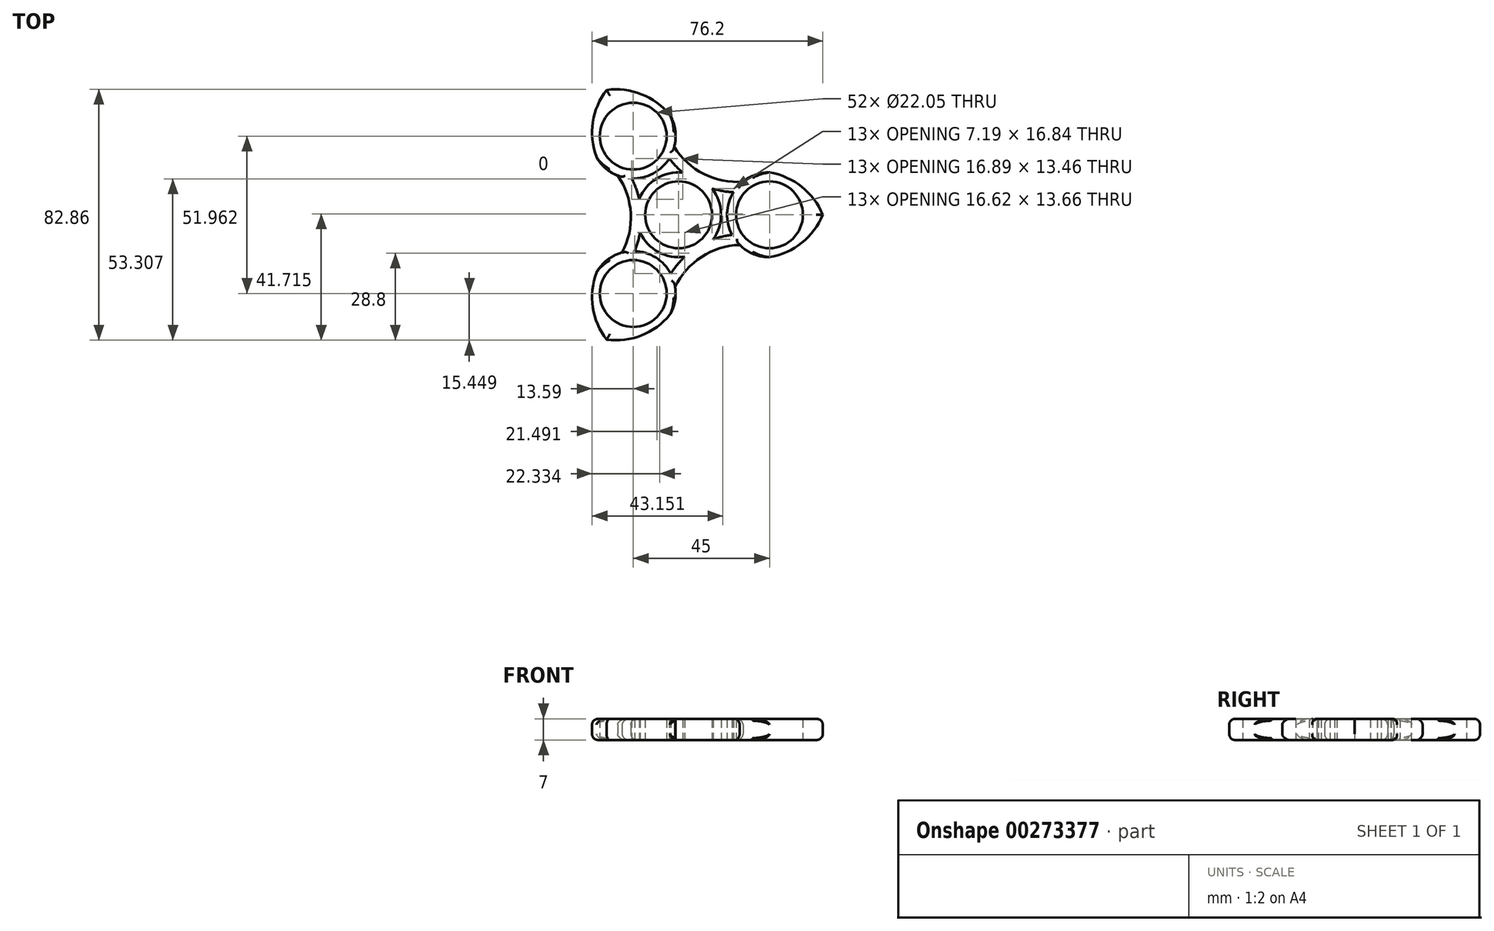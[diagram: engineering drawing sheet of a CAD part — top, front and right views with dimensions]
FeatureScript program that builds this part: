
annotation { "Feature Type Name" : "Feature", "Feature Type Description" : "" }
export const myFeature = defineFeature(function(context is Context, id is Id, definition is map)
    precondition{}
    {
        {
            var Q0;
            Q0=qCreatedBy(makeId("Top.planeOp"),FACE);
            var sketch = newSketch(context, id + "F0", { "sketchPlane" : qUnion([Q0])});
            skCircle(sketch, "E0", {"center": v(0, 0) * mm, "radius": 11.03 * mm});
            skCircle(sketch, "E1", {"center": v(30, 0) * mm, "radius": 11.03 * mm});
            skArc(sketch, "E2", {"start": v(11.4, -8.13) * mm, "mid": v(14, 0.36) * mm, "end": v(10.97, 8.7) * mm});
            skArc(sketch, "E3", {"start": v(30, 14) * mm, "mid": v(25.38, 13.22) * mm, "end": v(21.28, 10.95) * mm});
            skArc(sketch, "E4", {"start": v(47.61, 0) * mm, "mid": v(40.61, 9.27) * mm, "end": v(30, 14) * mm});
            skArc(sketch, "E5.MirrorCS", {"start": v(47.61, 0) * mm, "mid": v(40.61, -9.27) * mm, "end": v(30, -14) * mm});
            skArc(sketch, "E6.1.0", {"start": v(-27.12, 18.98) * mm, "mid": v(-24.14, 15.37) * mm, "end": v(-20.12, 12.95) * mm});
            skArc(sketch, "E6.1.1", {"start": v(-23.8, 41.23) * mm, "mid": v(-12.28, 39.8) * mm, "end": v(-2.88, 32.98) * mm});
            skCircle(sketch, "E6.1.2", {"center": v(-15, 25.98) * mm, "radius": 11.03 * mm});
            skArc(sketch, "E6.1.3", {"start": v(-23.8, 41.23) * mm, "mid": v(-28.34, 30.54) * mm, "end": v(-27.12, 18.98) * mm});
            skArc(sketch, "E6.2.0", {"start": v(-2.88, -32.98) * mm, "mid": v(-1.25, -28.59) * mm, "end": v(-1.15, -23.9) * mm});
            skArc(sketch, "E6.2.1", {"start": v(-23.8, -41.23) * mm, "mid": v(-28.34, -30.54) * mm, "end": v(-27.12, -18.98) * mm});
            skCircle(sketch, "E6.2.2", {"center": v(-15, -25.98) * mm, "radius": 11.03 * mm});
            skArc(sketch, "E6.2.3", {"start": v(-23.8, -41.23) * mm, "mid": v(-12.28, -39.8) * mm, "end": v(-2.88, -32.98) * mm});
            skArc(sketch, "E7.0", {"start": v(21.12, -6.42) * mm, "mid": v(21.08, -6.42) * mm, "end": v(21.03, -6.42) * mm});
            skArc(sketch, "E8.trimOffspring", {"start": v(17.66, -6.62) * mm, "mid": v(14.49, -7.2) * mm, "end": v(11.4, -8.13) * mm});
            skArc(sketch, "E9.trimOffspring", {"start": v(20.15, -9.95) * mm, "mid": v(24.68, -12.95) * mm, "end": v(30, -14) * mm});
            skArc(sketch, "E10.trimOffspring", {"start": v(-2.61, -19.46) * mm, "mid": v(-7.58, -14.1) * mm, "end": v(-14.57, -11.99) * mm});
            skArc(sketch, "E11.trimOffspring", {"start": v(2.05, -13.85) * mm, "mid": v(-0.46, -16.5) * mm, "end": v(-2.61, -19.46) * mm});
            skArc(sketch, "E12.1.0", {"start": v(10.97, 8.7) * mm, "mid": v(14.52, 7.85) * mm, "end": v(18.16, 7.47) * mm});
            skArc(sketch, "E12.1.2", {"start": v(-3.1, 18.6) * mm, "mid": v(-1.01, 16.14) * mm, "end": v(1.35, 13.94) * mm});
            skArc(sketch, "E12.2.0", {"start": v(-13.02, 5.15) * mm, "mid": v(-14.06, 8.65) * mm, "end": v(-15.54, 12) * mm});
            skArc(sketch, "E12.2.2", {"start": v(-14.57, -11.99) * mm, "mid": v(-13.47, -8.95) * mm, "end": v(-12.74, -5.8) * mm});
            skArc(sketch, "E13.trimOffspring", {"start": v(-12.74, -5.8) * mm, "mid": v(-6.69, -12.3) * mm, "end": v(2.05, -13.85) * mm});
            skArc(sketch, "E14.trimOffspring", {"start": v(1.35, 13.94) * mm, "mid": v(-7.3, 11.94) * mm, "end": v(-13.02, 5.15) * mm});
            skArc(sketch, "E15.trimOffspring", {"start": v(-15.54, 12) * mm, "mid": v(-8.43, 13.62) * mm, "end": v(-3.1, 18.6) * mm});
            skArc(sketch, "E16.trimOffspring", {"start": v(-1.46, 22.43) * mm, "mid": v(-1.12, 27.84) * mm, "end": v(-2.88, 32.98) * mm});
            skArc(sketch, "E17.trimOffspring", {"start": v(18.16, 7.47) * mm, "mid": v(16, 0.49) * mm, "end": v(17.66, -6.62) * mm});
            skArc(sketch, "E18.trimOffspring", {"start": v(-18.7, -12.48) * mm, "mid": v(-23.55, -14.9) * mm, "end": v(-27.12, -18.98) * mm});
            skArc(sketch, "E19", {"start": v(-1.46, 22.43) * mm, "mid": v(8.3, 13.48) * mm, "end": v(21.28, 10.95) * mm});
            skArc(sketch, "E20.1.0", {"start": v(-18.7, -12.48) * mm, "mid": v(-15.82, 0.44) * mm, "end": v(-20.12, 12.95) * mm});
            skArc(sketch, "E20.2.0", {"start": v(20.15, -9.95) * mm, "mid": v(7.53, -13.92) * mm, "end": v(-1.15, -23.9) * mm});
            skSolve(sketch);
        }
        {
            var Q0;
            Q0=makeQuery(id+"F0.imprint","IMPRINT",FACE,{"disambiguationData":[TD([[makeQuery(id+"F0.imprint","IMPRINT",EDGE,{"derivedFrom":sQuery(id+"F0.wireOp",EDGE,"E0")}),-1.0]])]});
            extrude(context, id + "F1", {"entities" : qUnion([Q0]), "depth" : 7 * mm});
        }
        {
            var Q0;
            Q0=makeQuery(id+"F1.opExtrude","CAP_EDGE",EDGE,{"disambiguationData":[OSD([sQuery(id+"F0.wireOp",EDGE,"E20.1.0")])],"isStart":false});
            var Q1;
            Q1=makeQuery(id+"F1.opExtrude","CAP_EDGE",EDGE,{"disambiguationData":[OSD([sQuery(id+"F0.wireOp",EDGE,"E6.1.1")])],"isStart":false});
            var Q2;
            Q2=makeQuery(id+"F1.opExtrude","CAP_EDGE",EDGE,{"disambiguationData":[OSD([sQuery(id+"F0.wireOp",EDGE,"E6.1.3")])],"isStart":false});
            var Q3;
            Q3=makeQuery(id+"F1.opExtrude","CAP_EDGE",EDGE,{"disambiguationData":[OSD([sQuery(id+"F0.wireOp",EDGE,"E19")])],"isStart":false});
            var Q4;
            Q4=makeQuery(id+"F1.opExtrude","CAP_EDGE",EDGE,{"disambiguationData":[OSD([sQuery(id+"F0.wireOp",EDGE,"E20.2.0")])],"isStart":false});
            var Q5;
            Q5=makeQuery(id+"F1.opExtrude","CAP_EDGE",EDGE,{"disambiguationData":[OSD([sQuery(id+"F0.wireOp",EDGE,"E6.2.3")])],"isStart":false});
            var Q6;
            Q6=makeQuery(id+"F1.opExtrude","CAP_EDGE",EDGE,{"disambiguationData":[OSD([sQuery(id+"F0.wireOp",EDGE,"E6.2.1")])],"isStart":false});
            var Q7;
            Q7=makeQuery(id+"F1.opExtrude","CAP_EDGE",EDGE,{"disambiguationData":[OSD([sQuery(id+"F0.wireOp",EDGE,"E5.MirrorCS")])],"isStart":false});
            var Q8;
            Q8=makeQuery(id+"F1.opExtrude","CAP_EDGE",EDGE,{"disambiguationData":[OSD([sQuery(id+"F0.wireOp",EDGE,"E4")])],"isStart":false});
            var Q9;
            Q9=makeQuery(id+"F1.opExtrude","CAP_EDGE",EDGE,{"disambiguationData":[OSD([sQuery(id+"F0.wireOp",EDGE,"E20.2.0")])],"isStart":true});
            var Q10;
            Q10=makeQuery(id+"F1.opExtrude","CAP_EDGE",EDGE,{"disambiguationData":[OSD([sQuery(id+"F0.wireOp",EDGE,"E19")])],"isStart":true});
            var Q11;
            Q11=makeQuery(id+"F1.opExtrude","CAP_EDGE",EDGE,{"disambiguationData":[OSD([sQuery(id+"F0.wireOp",EDGE,"E20.1.0")])],"isStart":true});
            var Q12;
            Q12=makeQuery(id+"F1.opExtrude","CAP_EDGE",EDGE,{"disambiguationData":[OSD([sQuery(id+"F0.wireOp",EDGE,"E6.2.1")])],"isStart":true});
            var Q13;
            Q13=makeQuery(id+"F1.opExtrude","CAP_EDGE",EDGE,{"disambiguationData":[OSD([sQuery(id+"F0.wireOp",EDGE,"E6.1.3")])],"isStart":true});
            var Q14;
            Q14=makeQuery(id+"F1.opExtrude","CAP_EDGE",EDGE,{"disambiguationData":[OSD([sQuery(id+"F0.wireOp",EDGE,"E6.1.1")])],"isStart":true});
            var Q15;
            Q15=makeQuery(id+"F1.opExtrude","CAP_EDGE",EDGE,{"disambiguationData":[OSD([sQuery(id+"F0.wireOp",EDGE,"E4")])],"isStart":true});
            var Q16;
            Q16=makeQuery(id+"F1.opExtrude","CAP_EDGE",EDGE,{"disambiguationData":[OSD([sQuery(id+"F0.wireOp",EDGE,"E5.MirrorCS")])],"isStart":true});
            var Q17;
            Q17=makeQuery(id+"F1.opExtrude","CAP_EDGE",EDGE,{"disambiguationData":[OSD([sQuery(id+"F0.wireOp",EDGE,"E6.2.3")])],"isStart":true});
            fillet(context, id + "F2", {"entities" : qUnion([Q0, Q1, Q2, Q3, Q4, Q5, Q6, Q7, Q8, Q9, Q10, Q11, Q12, Q13, Q14, Q15, Q16, Q17]), "radius" : 2 * mm, "allowEdgeOverflow" : false});
        }
        {
            var Q0;
            Q0=makeQuery(id+"F1.opExtrude","CAP_EDGE",EDGE,{"disambiguationData":[OSD([sQuery(id+"F0.wireOp",EDGE,"E16.trimOffspring")])],"isStart":false});
            var Q1;
            Q1=makeQuery(id+"F1.opExtrude","CAP_EDGE",EDGE,{"disambiguationData":[OSD([sQuery(id+"F0.wireOp",EDGE,"E6.1.0")])],"isStart":false});
            var Q2;
            Q2=makeQuery(id+"F1.opExtrude","CAP_EDGE",EDGE,{"disambiguationData":[OSD([sQuery(id+"F0.wireOp",EDGE,"E18.trimOffspring")])],"isStart":false});
            var Q3;
            Q3=makeQuery(id+"F1.opExtrude","CAP_EDGE",EDGE,{"disambiguationData":[OSD([sQuery(id+"F0.wireOp",EDGE,"E6.2.0")])],"isStart":false});
            var Q4;
            Q4=makeQuery(id+"F1.opExtrude","CAP_EDGE",EDGE,{"disambiguationData":[OSD([sQuery(id+"F0.wireOp",EDGE,"E9.trimOffspring")])],"isStart":false});
            var Q5;
            Q5=makeQuery(id+"F1.opExtrude","CAP_EDGE",EDGE,{"disambiguationData":[OSD([sQuery(id+"F0.wireOp",EDGE,"E3")])],"isStart":false});
            fillet(context, id + "F3", {"entities" : qUnion([Q0, Q1, Q2, Q3, Q4, Q5]), "radius" : .6 * mm, "tangentPropagation" : true, "allowEdgeOverflow" : false});
        }
    });
